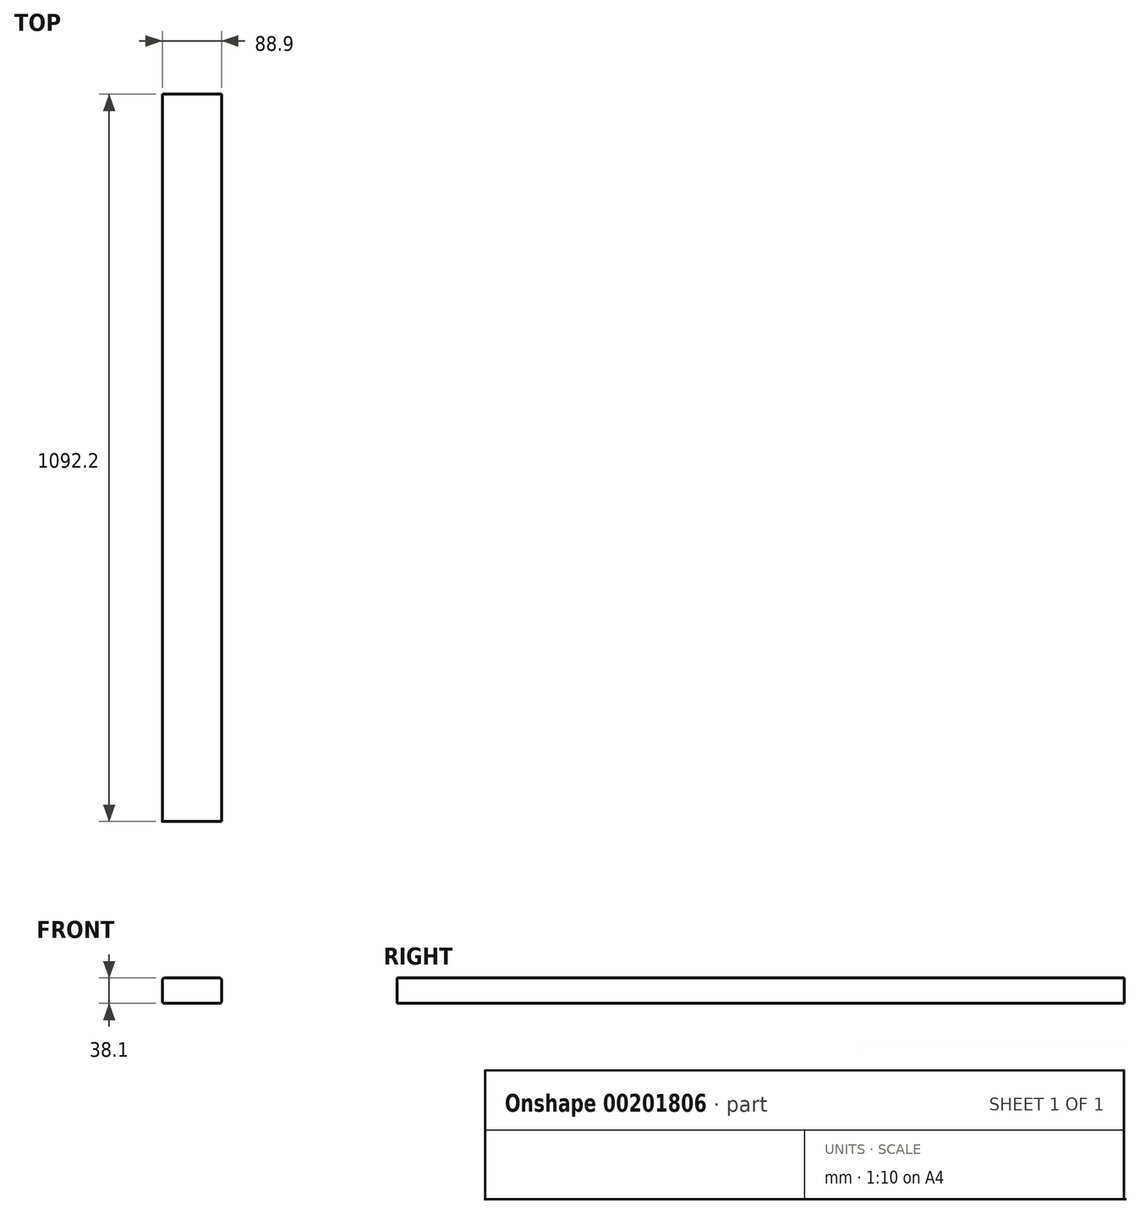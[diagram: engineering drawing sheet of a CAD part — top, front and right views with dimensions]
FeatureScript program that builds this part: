
annotation { "Feature Type Name" : "Feature", "Feature Type Description" : "" }
export const myFeature = defineFeature(function(context is Context, id is Id, definition is map)
    precondition{}
    {
        {
            var Q0;
            Q0=qCreatedBy(makeId("Front.planeOp"),FACE);
            var sketch = newSketch(context, id + "F0", { "sketchPlane" : qUnion([Q0])});
            skLineSegment(sketch, "E0.bottom", {"start": v(41.28, -19.05) * mm, "end": v(-41.28, -19.05) * mm});
            skLineSegment(sketch, "E0.top", {"start": v(41.28, 19.05) * mm, "end": v(-41.28, 19.05) * mm});
            skLineSegment(sketch, "E0.left", {"start": v(44.45, -15.87) * mm, "end": v(44.45, 15.88) * mm});
            skLineSegment(sketch, "E0.right", {"start": v(-44.45, -15.88) * mm, "end": v(-44.45, 15.88) * mm});
            skPoint(sketch, "E0.middle", {"position": v(0, 0) * mm});
            skPoint(sketch, "E1.visualSharp", {"position": v(-44.45, 19.05) * mm});
            skArc(sketch, "E1.filletArc", {"start": v(-41.28, 19.05) * mm, "mid": v(-43.52, 18.12) * mm, "end": v(-44.45, 15.88) * mm});
            skPoint(sketch, "E2.visualSharp", {"position": v(-44.45, -19.05) * mm});
            skArc(sketch, "E2.filletArc", {"start": v(-44.45, -15.88) * mm, "mid": v(-43.52, -18.12) * mm, "end": v(-41.28, -19.05) * mm});
            skPoint(sketch, "E3.visualSharp", {"position": v(44.45, -19.05) * mm});
            skArc(sketch, "E3.filletArc", {"start": v(41.28, -19.05) * mm, "mid": v(43.52, -18.12) * mm, "end": v(44.45, -15.87) * mm});
            skPoint(sketch, "E4.visualSharp", {"position": v(44.45, 19.05) * mm});
            skArc(sketch, "E4.filletArc", {"start": v(44.45, 15.88) * mm, "mid": v(43.52, 18.12) * mm, "end": v(41.28, 19.05) * mm});
            skSolve(sketch);
        }
        {
            var Q0;
            Q0=makeQuery(id+"F0.imprint","IMPRINT",FACE,{"disambiguationData":[TD([[makeQuery(id+"F0.imprint","IMPRINT",EDGE,{"derivedFrom":sQuery(id+"F0.wireOp",EDGE,"E0.bottom")}),-1.0]])]});
            extrude(context, id + "F1", {"entities" : qUnion([Q0]), "depth" : 1092.2 * mm});
        }
    });
